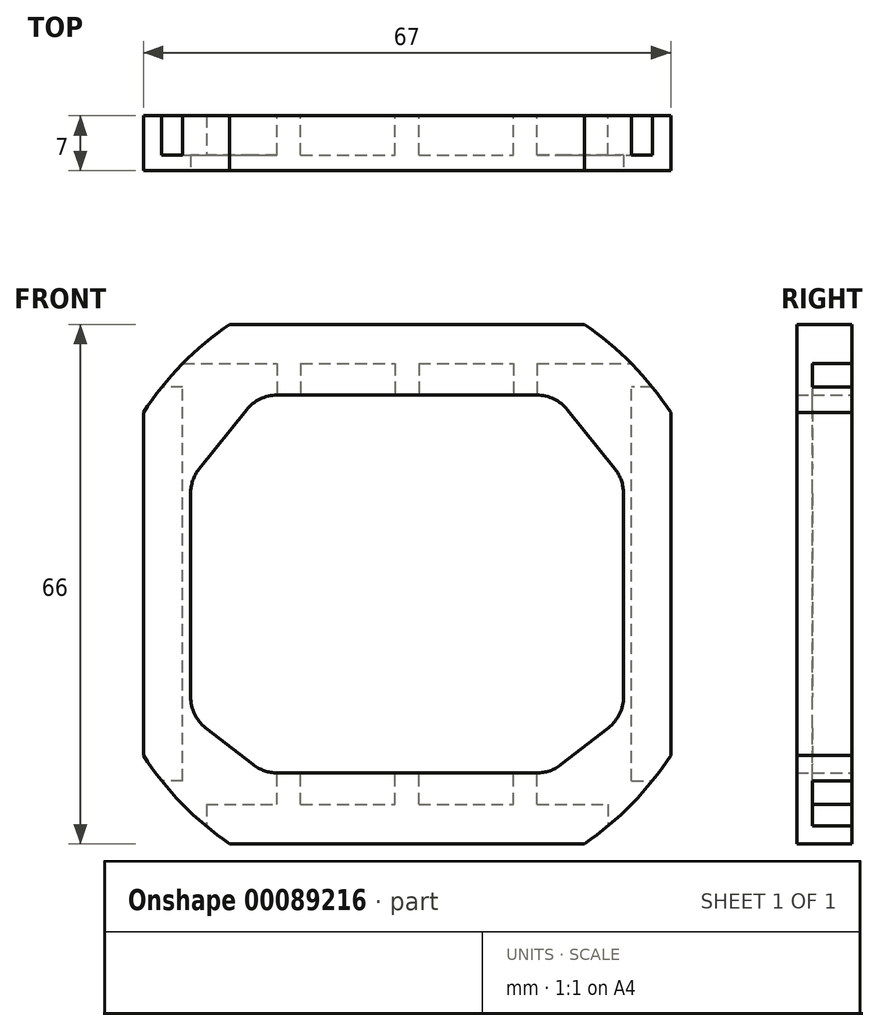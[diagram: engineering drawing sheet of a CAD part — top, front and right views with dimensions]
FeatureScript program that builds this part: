
annotation { "Feature Type Name" : "Feature", "Feature Type Description" : "" }
export const myFeature = defineFeature(function(context is Context, id is Id, definition is map)
    precondition{}
    {
        {
            var Q0;
            Q0=qCreatedBy(makeId("Front.planeOp"),FACE);
            var sketch = newSketch(context, id + "F0", { "sketchPlane" : qUnion([Q0])});
            skLineSegment(sketch, "E0.bottom", {"start": v(0, 0) * mm, "end": v(12, 0) * mm});
            skLineSegment(sketch, "E0.top", {"start": v(0, 56) * mm, "end": v(12, 56) * mm});
            skLineSegment(sketch, "E0.left", {"start": v(0, 0) * mm, "end": v(0, 56) * mm});
            skLineSegment(sketch, "E0.right", {"start": v(57, 0) * mm, "end": v(57, 56) * mm});
            skLineSegment(sketch, "E1.bottom", {"start": v(-5, 61) * mm, "end": v(62, 61) * mm});
            skLineSegment(sketch, "E1.top", {"start": v(-5, -5) * mm, "end": v(62, -5) * mm});
            skLineSegment(sketch, "E1.left", {"start": v(-5, 61) * mm, "end": v(-5, -5) * mm});
            skLineSegment(sketch, "E1.right", {"start": v(62, 61) * mm, "end": v(62, -5) * mm});
            skLineSegment(sketch, "E2.top", {"start": v(12, 52) * mm, "end": v(15, 52) * mm});
            skLineSegment(sketch, "E2.left", {"start": v(12, 56) * mm, "end": v(12, 52) * mm});
            skLineSegment(sketch, "E2.right", {"start": v(15, 56) * mm, "end": v(15, 52) * mm});
            skPoint(sketch, "E3.oppositeSnap0", {"position": v(30, 56) * mm});
            skLineSegment(sketch, "E3.top", {"start": v(27, 52) * mm, "end": v(30, 52) * mm});
            skLineSegment(sketch, "E3.left", {"start": v(27, 56) * mm, "end": v(27, 52) * mm});
            skLineSegment(sketch, "E3.right", {"start": v(30, 56) * mm, "end": v(30, 52) * mm});
            skLineSegment(sketch, "E4.top", {"start": v(42, 52) * mm, "end": v(45, 52) * mm});
            skLineSegment(sketch, "E4.left", {"start": v(42, 56) * mm, "end": v(42, 52) * mm});
            skLineSegment(sketch, "E4.right", {"start": v(45, 56) * mm, "end": v(45, 52) * mm});
            skLineSegment(sketch, "E5.top", {"start": v(12, 4) * mm, "end": v(15, 4) * mm});
            skLineSegment(sketch, "E5.left", {"start": v(12, 0) * mm, "end": v(12, 4) * mm});
            skLineSegment(sketch, "E5.right", {"start": v(15, 0) * mm, "end": v(15, 4) * mm});
            skLineSegment(sketch, "E6.top", {"start": v(27, 4) * mm, "end": v(30, 4) * mm});
            skLineSegment(sketch, "E6.left", {"start": v(27, 0) * mm, "end": v(27, 4) * mm});
            skLineSegment(sketch, "E6.right", {"start": v(30, 0) * mm, "end": v(30, 4) * mm});
            skLineSegment(sketch, "E7.top", {"start": v(42, 4) * mm, "end": v(45, 4) * mm});
            skLineSegment(sketch, "E7.left", {"start": v(42, 0) * mm, "end": v(42, 4) * mm});
            skLineSegment(sketch, "E7.right", {"start": v(45, 0) * mm, "end": v(45, 4) * mm});
            skLineSegment(sketch, "E8.trimOffspring", {"start": v(15, 56) * mm, "end": v(27, 56) * mm});
            skLineSegment(sketch, "E9.trimOffspring", {"start": v(30, 56) * mm, "end": v(42, 56) * mm});
            skLineSegment(sketch, "E10.trimOffspring", {"start": v(45, 56) * mm, "end": v(57, 56) * mm});
            skLineSegment(sketch, "E11.trimOffspring", {"start": v(30, 0) * mm, "end": v(42, 0) * mm});
            skLineSegment(sketch, "E12.trimOffspring", {"start": v(15, 0) * mm, "end": v(27, 0) * mm});
            skLineSegment(sketch, "E13.trimOffspring", {"start": v(45, 0) * mm, "end": v(57, 0) * mm});
            skSolve(sketch);
        }
        {
            var Q0;
            Q0=makeQuery(id+"F0.imprint","IMPRINT",FACE,{"disambiguationData":[TD([[makeQuery(id+"F0.imprint","IMPRINT",EDGE,{"derivedFrom":sQuery(id+"F0.wireOp",EDGE,"E0.bottom")}),-1.0]])]});
            extrude(context, id + "F1", {"entities" : qUnion([Q0]), "depth" : 5 * mm});
        }
        {
            var Q0;
            Q0=makeQuery(id+"F1.opExtrude","CAP_FACE",FACE,{"disambiguationData":[OSD([sQuery(id+"F0.wireOp",EDGE,"E0.bottom"),sQuery(id+"F0.wireOp",EDGE,"E0.top"),sQuery(id+"F0.wireOp",EDGE,"E0.left"),sQuery(id+"F0.wireOp",EDGE,"E0.right"),sQuery(id+"F0.wireOp",EDGE,"E1.bottom"),sQuery(id+"F0.wireOp",EDGE,"E1.top"),sQuery(id+"F0.wireOp",EDGE,"E1.left"),sQuery(id+"F0.wireOp",EDGE,"E1.right"),sQuery(id+"F0.wireOp",EDGE,"E2.top"),sQuery(id+"F0.wireOp",EDGE,"E2.left"),sQuery(id+"F0.wireOp",EDGE,"E2.right"),sQuery(id+"F0.wireOp",EDGE,"E3.top"),sQuery(id+"F0.wireOp",EDGE,"E3.left"),sQuery(id+"F0.wireOp",EDGE,"E3.right"),sQuery(id+"F0.wireOp",EDGE,"E4.top"),sQuery(id+"F0.wireOp",EDGE,"E4.left"),sQuery(id+"F0.wireOp",EDGE,"E4.right"),sQuery(id+"F0.wireOp",EDGE,"E5.top"),sQuery(id+"F0.wireOp",EDGE,"E5.left"),sQuery(id+"F0.wireOp",EDGE,"E5.right"),sQuery(id+"F0.wireOp",EDGE,"E6.top"),sQuery(id+"F0.wireOp",EDGE,"E6.left"),sQuery(id+"F0.wireOp",EDGE,"E6.right"),sQuery(id+"F0.wireOp",EDGE,"E7.top"),sQuery(id+"F0.wireOp",EDGE,"E7.left"),sQuery(id+"F0.wireOp",EDGE,"E7.right"),sQuery(id+"F0.wireOp",EDGE,"E8.trimOffspring"),sQuery(id+"F0.wireOp",EDGE,"E9.trimOffspring"),sQuery(id+"F0.wireOp",EDGE,"E10.trimOffspring"),sQuery(id+"F0.wireOp",EDGE,"E11.trimOffspring"),sQuery(id+"F0.wireOp",EDGE,"E12.trimOffspring"),sQuery(id+"F0.wireOp",EDGE,"E13.trimOffspring")])],"isStart":false});
            var sketch = newSketch(context, id + "F2", { "sketchPlane" : qUnion([Q0])});
            skLineSegment(sketch, "E14.bottom", {"start": v(-5, 61) * mm, "end": v(62, 61) * mm});
            skLineSegment(sketch, "E14.top", {"start": v(-5, -5) * mm, "end": v(62, -5) * mm});
            skLineSegment(sketch, "E14.left", {"start": v(-5, 61) * mm, "end": v(-5, -5) * mm});
            skLineSegment(sketch, "E14.right", {"start": v(62, 61) * mm, "end": v(62, -5) * mm});
            skLineSegment(sketch, "E15.bottom", {"start": v(12, 52) * mm, "end": v(15, 52) * mm});
            skLineSegment(sketch, "E15.top", {"start": v(12, 4) * mm, "end": v(15, 4) * mm});
            skLineSegment(sketch, "E15.left", {"start": v(12, 52) * mm, "end": v(12, 4) * mm});
            skLineSegment(sketch, "E15.right", {"start": v(15, 52) * mm, "end": v(15, 4) * mm});
            skLineSegment(sketch, "E16.bottom", {"start": v(27, 52) * mm, "end": v(30, 52) * mm});
            skLineSegment(sketch, "E16.top", {"start": v(27, 4) * mm, "end": v(30, 4) * mm});
            skLineSegment(sketch, "E16.left", {"start": v(27, 52) * mm, "end": v(27, 4) * mm});
            skLineSegment(sketch, "E16.right", {"start": v(30, 52) * mm, "end": v(30, 4) * mm});
            skLineSegment(sketch, "E17.bottom", {"start": v(42, 52) * mm, "end": v(45, 52) * mm});
            skLineSegment(sketch, "E17.top", {"start": v(42, 4) * mm, "end": v(45, 4) * mm});
            skLineSegment(sketch, "E17.left", {"start": v(42, 52) * mm, "end": v(42, 4) * mm});
            skLineSegment(sketch, "E17.right", {"start": v(45, 52) * mm, "end": v(45, 4) * mm});
            skSolve(sketch);
        }
        {
            var Q0;
            Q0=makeQuery(id+"F2.imprint","IMPRINT",FACE,{"disambiguationData":[TD([[makeQuery(id+"F2.imprint","IMPRINT",EDGE,{"derivedFrom":sQuery(id+"F2.wireOp",EDGE,"E14.bottom")}),-1.0]])]});
            var Q1;
            Q1=makeQuery(id+"F2.imprint","IMPRINT",FACE,{"disambiguationData":[TD([[makeQuery(id+"F2.imprint","IMPRINT",EDGE,{"derivedFrom":sQuery(id+"F2.wireOp",EDGE,"E15.left")}),-1.0]])]});
            var Q2;
            Q2=makeQuery(id+"F2.imprint","IMPRINT",FACE,{"disambiguationData":[TD([[makeQuery(id+"F2.imprint","IMPRINT",EDGE,{"derivedFrom":sQuery(id+"F2.wireOp",EDGE,"E15.right")}),1.0]])]});
            var Q3;
            Q3=makeQuery(id+"F2.imprint","IMPRINT",FACE,{"disambiguationData":[TD([[makeQuery(id+"F2.imprint","IMPRINT",EDGE,{"derivedFrom":sQuery(id+"F2.wireOp",EDGE,"E16.right")}),1.0]])]});
            var Q4;
            Q4=makeQuery(id+"F2.imprint","IMPRINT",FACE,{"disambiguationData":[TD([[makeQuery(id+"F2.imprint","IMPRINT",EDGE,{"derivedFrom":sQuery(id+"F2.wireOp",EDGE,"E17.right")}),1.0]])]});
            extrude(context, id + "F3", {"entities" : qUnion([Q0, Q1, Q2, Q3, Q4]), "operationType" : NewBodyOperationType.ADD, "depth" : 2 * mm});
        }
        {
            var Q0;
            Q0=makeQuery(id+"F3.opExtrude","CAP_FACE",FACE,{"disambiguationData":[OSD([sQuery(id+"F2.wireOp",EDGE,"E14.bottom"),sQuery(id+"F2.wireOp",EDGE,"E14.top"),sQuery(id+"F2.wireOp",EDGE,"E14.left"),sQuery(id+"F2.wireOp",EDGE,"E14.right"),sQuery(id+"F2.wireOp",EDGE,"E15.bottom"),sQuery(id+"F2.wireOp",EDGE,"E15.top"),sQuery(id+"F2.wireOp",EDGE,"E15.left"),sQuery(id+"F2.wireOp",EDGE,"E15.right"),sQuery(id+"F2.wireOp",EDGE,"E16.bottom"),sQuery(id+"F2.wireOp",EDGE,"E16.top"),sQuery(id+"F2.wireOp",EDGE,"E16.left"),sQuery(id+"F2.wireOp",EDGE,"E16.right"),sQuery(id+"F2.wireOp",EDGE,"E17.bottom"),sQuery(id+"F2.wireOp",EDGE,"E17.top"),sQuery(id+"F2.wireOp",EDGE,"E17.left"),sQuery(id+"F2.wireOp",EDGE,"E17.right")])],"isStart":false});
            var sketch = newSketch(context, id + "F4", { "sketchPlane" : qUnion([Q0])});
            skLineSegment(sketch, "E18.left", {"start": v(56, 39.5) * mm, "end": v(56, 13.7) * mm});
            skLineSegment(sketch, "E19.right", {"start": v(1, 39.5) * mm, "end": v(1, 13.7) * mm});
            skPoint(sketch, "E20.visualSharp", {"position": v(1, 41) * mm});
            skPoint(sketch, "E21.visualSharp", {"position": v(10, 41) * mm});
            skPoint(sketch, "E22.visualSharp", {"position": v(10, 19) * mm});
            skPoint(sketch, "E23.visualSharp", {"position": v(1, 19) * mm});
            skPoint(sketch, "E24.visualSharp", {"position": v(17.5, 41) * mm});
            skPoint(sketch, "E25.visualSharp", {"position": v(26.5, 41) * mm});
            skPoint(sketch, "E26.visualSharp", {"position": v(26.5, 19) * mm});
            skPoint(sketch, "E27.visualSharp", {"position": v(17.5, 19) * mm});
            skPoint(sketch, "E28.visualSharp", {"position": v(33.5, 19) * mm});
            skPoint(sketch, "E29.visualSharp", {"position": v(42.5, 19) * mm});
            skPoint(sketch, "E30.visualSharp", {"position": v(42.5, 41) * mm});
            skPoint(sketch, "E31.visualSharp", {"position": v(33.5, 41) * mm});
            skPoint(sketch, "E32.visualSharp", {"position": v(49.5, 41) * mm});
            skPoint(sketch, "E33.visualSharp", {"position": v(56, 19) * mm});
            skPoint(sketch, "E34.visualSharp", {"position": v(56, 41) * mm});
            skPoint(sketch, "E35.visualSharp", {"position": v(49.5, 19) * mm});
            skLineSegment(sketch, "E36", {"start": v(2.1, 42.62) * mm, "end": v(8.1, 50.12) * mm});
            skLineSegment(sketch, "E37", {"start": v(12, 52) * mm, "end": v(45, 52) * mm});
            skLineSegment(sketch, "E38", {"start": v(48.9, 50.12) * mm, "end": v(54.9, 42.62) * mm});
            skLineSegment(sketch, "E39", {"start": v(54.08, 9.75) * mm, "end": v(48.08, 5.06) * mm});
            skLineSegment(sketch, "E40", {"start": v(45, 4) * mm, "end": v(12, 4) * mm});
            skLineSegment(sketch, "E41", {"start": v(8.92, 5.06) * mm, "end": v(2.92, 9.75) * mm});
            skPoint(sketch, "E42.visualSharp", {"position": v(1, 41.25) * mm});
            skArc(sketch, "E42.filletArc", {"start": v(2.1, 42.62) * mm, "mid": v(1.28, 41.16) * mm, "end": v(1, 39.5) * mm});
            skPoint(sketch, "E43.visualSharp", {"position": v(1, 11.25) * mm});
            skArc(sketch, "E43.filletArc", {"start": v(1, 13.7) * mm, "mid": v(1.5, 11.5) * mm, "end": v(2.92, 9.75) * mm});
            skPoint(sketch, "E44.visualSharp", {"position": v(56, 41.25) * mm});
            skArc(sketch, "E44.filletArc", {"start": v(56, 39.5) * mm, "mid": v(55.72, 41.16) * mm, "end": v(54.9, 42.62) * mm});
            skPoint(sketch, "E45.visualSharp", {"position": v(56, 11.25) * mm});
            skArc(sketch, "E45.filletArc", {"start": v(54.08, 9.75) * mm, "mid": v(55.5, 11.5) * mm, "end": v(56, 13.7) * mm});
            skArc(sketch, "E46.filletArc", {"start": v(48.9, 50.12) * mm, "mid": v(47.17, 51.5) * mm, "end": v(45, 52) * mm});
            skArc(sketch, "E47.filletArc", {"start": v(12, 52) * mm, "mid": v(9.83, 51.5) * mm, "end": v(8.1, 50.12) * mm});
            skArc(sketch, "E48.filletArc", {"start": v(8.92, 5.06) * mm, "mid": v(10.37, 4.27) * mm, "end": v(12, 4) * mm});
            skArc(sketch, "E49.filletArc", {"start": v(45, 4) * mm, "mid": v(46.63, 4.27) * mm, "end": v(48.08, 5.06) * mm});
            skSolve(sketch);
        }
        {
            var Q0;
            Q0=makeQuery(id+"F4.imprint","IMPRINT",FACE,{"disambiguationData":[TD([[makeQuery(id+"F4.imprint","IMPRINT",EDGE,{"derivedFrom":sQuery(id+"F4.wireOp",EDGE,"E19.right")}),1.0]])]});
            var Q1;
            {var subQ1=makeQuery(id+"F3.opExtrude","CAP_EDGE",EDGE,{"disambiguationData":[OSD([sQuery(id+"F2.wireOp",EDGE,"E15.right")])],"isStart":false});Q1=makeQuery(id+"F4.imprint","IMPRINT",FACE,{"disambiguationData":[TD([[makeQuery(id+"F4.imprint","IMPRINT",EDGE,{"derivedFrom":subQ1}),1.0]])]});}
            var Q2;
            {var subQ1=makeQuery(id+"F3.opExtrude","CAP_EDGE",EDGE,{"disambiguationData":[OSD([sQuery(id+"F2.wireOp",EDGE,"E16.right")])],"isStart":false});Q2=makeQuery(id+"F4.imprint","IMPRINT",FACE,{"disambiguationData":[TD([[makeQuery(id+"F4.imprint","IMPRINT",EDGE,{"derivedFrom":subQ1}),1.0]])]});}
            var Q3;
            Q3=makeQuery(id+"F4.imprint","IMPRINT",FACE,{"disambiguationData":[TD([[makeQuery(id+"F4.imprint","IMPRINT",EDGE,{"derivedFrom":sQuery(id+"F4.wireOp",EDGE,"E18.left")}),-1.0]])]});
            extrude(context, id + "F5", {"entities" : qUnion([Q0, Q1, Q2, Q3]), "operationType" : NewBodyOperationType.REMOVE, "endBound" : BoundingType.THROUGH_ALL, "oppositeDirection" : true, "depth" : 25 * mm});
        }
        {
            var Q0;
            Q0=makeQuery(id+"F3.opExtrude","CAP_FACE",FACE,{"disambiguationData":[OSD([sQuery(id+"F2.wireOp",EDGE,"E14.bottom"),sQuery(id+"F2.wireOp",EDGE,"E14.top"),sQuery(id+"F2.wireOp",EDGE,"E14.left"),sQuery(id+"F2.wireOp",EDGE,"E14.right"),sQuery(id+"F2.wireOp",EDGE,"E15.bottom"),sQuery(id+"F2.wireOp",EDGE,"E15.top"),sQuery(id+"F2.wireOp",EDGE,"E15.left"),sQuery(id+"F2.wireOp",EDGE,"E15.right"),sQuery(id+"F2.wireOp",EDGE,"E16.bottom"),sQuery(id+"F2.wireOp",EDGE,"E16.top"),sQuery(id+"F2.wireOp",EDGE,"E16.left"),sQuery(id+"F2.wireOp",EDGE,"E16.right"),sQuery(id+"F2.wireOp",EDGE,"E17.bottom"),sQuery(id+"F2.wireOp",EDGE,"E17.top"),sQuery(id+"F2.wireOp",EDGE,"E17.left"),sQuery(id+"F2.wireOp",EDGE,"E17.right")])],"isStart":false});
            var sketch = newSketch(context, id + "F6", { "sketchPlane" : qUnion([Q0])});
            skArc(sketch, "E50", {"start": v(5.98, 61) * mm, "mid": v(-0.07, 55.93) * mm, "end": v(-5, 49.77) * mm});
            skLineSegment(sketch, "E51", {"start": v(-5, 49.77) * mm, "end": v(-5, 6.23) * mm});
            skLineSegment(sketch, "E52", {"start": v(5.98, 61) * mm, "end": v(51.02, 61) * mm});
            skLineSegment(sketch, "E53", {"start": v(62, 49.77) * mm, "end": v(62, 6.23) * mm});
            skLineSegment(sketch, "E54", {"start": v(5.98, -5) * mm, "end": v(51.02, -5) * mm});
            skArc(sketch, "E55.trimOffspring", {"start": v(-5, 6.23) * mm, "mid": v(-0.07, 0.07) * mm, "end": v(5.98, -5) * mm});
            skArc(sketch, "E56.trimOffspring", {"start": v(51.02, -5) * mm, "mid": v(57.07, 0.07) * mm, "end": v(62, 6.23) * mm});
            skArc(sketch, "E57.trimOffspring", {"start": v(62, 49.77) * mm, "mid": v(57.07, 55.93) * mm, "end": v(51.02, 61) * mm});
            skSolve(sketch);
        }
        {
            var Q0;
            {var subQ0=sQuery(id+"F6.wireOp",EDGE,"E50");Q0=makeQuery(id+"F6.imprint","IMPRINT",FACE,{"disambiguationData":[TD([[makeQuery(id+"F6.imprint","IMPRINT",EDGE,{"derivedFrom":subQ0}),-1.0]])]});}
            var Q1;
            {var subQ0=sQuery(id+"F6.wireOp",EDGE,"E57.trimOffspring");Q1=makeQuery(id+"F6.imprint","IMPRINT",FACE,{"disambiguationData":[TD([[makeQuery(id+"F6.imprint","IMPRINT",EDGE,{"derivedFrom":subQ0}),-1.0]])]});}
            var Q2;
            {var subQ0=sQuery(id+"F6.wireOp",EDGE,"E56.trimOffspring");Q2=makeQuery(id+"F6.imprint","IMPRINT",FACE,{"disambiguationData":[TD([[makeQuery(id+"F6.imprint","IMPRINT",EDGE,{"derivedFrom":subQ0}),-1.0]])]});}
            var Q3;
            {var subQ0=sQuery(id+"F6.wireOp",EDGE,"E55.trimOffspring");Q3=makeQuery(id+"F6.imprint","IMPRINT",FACE,{"disambiguationData":[TD([[makeQuery(id+"F6.imprint","IMPRINT",EDGE,{"derivedFrom":subQ0}),-1.0]])]});}
            extrude(context, id + "F7", {"entities" : qUnion([Q0, Q1, Q2, Q3]), "operationType" : NewBodyOperationType.REMOVE, "endBound" : BoundingType.THROUGH_ALL, "oppositeDirection" : true, "depth" : 25 * mm});
        }
        {
            var Q0;
            {var subQ0=sQuery(id+"F0.wireOp",EDGE,"E4.left");var subQ1=sQuery(id+"F0.wireOp",EDGE,"E2.top");var subQ2=sQuery(id+"F0.wireOp",EDGE,"E8.trimOffspring");var subQ3=sQuery(id+"F0.wireOp",EDGE,"E4.top");var subQ4=sQuery(id+"F0.wireOp",EDGE,"E3.right");var subQ5=sQuery(id+"F0.wireOp",EDGE,"E3.left");var subQ6=sQuery(id+"F0.wireOp",EDGE,"E3.top");var subQ7=sQuery(id+"F0.wireOp",EDGE,"E2.right");var subQ8=sQuery(id+"F0.wireOp",EDGE,"E1.bottom");var subQ9=sQuery(id+"F0.wireOp",EDGE,"E0.top");var subQ10=sQuery(id+"F0.wireOp",EDGE,"E2.left");var subQ11=sQuery(id+"F0.wireOp",EDGE,"E4.right");var subQ12=sQuery(id+"F0.wireOp",EDGE,"E9.trimOffspring");var subQ13=sQuery(id+"F0.wireOp",EDGE,"E10.trimOffspring");Q0=makeQuery(id+"F7.boolean.opBoolean","SPLIT",FACE,{"disambiguationData":[TD([makeQuery(id+"F1.opExtrude","SWEPT_FACE",FACE,{"disambiguationData":[OSD([subQ9])]})])],"derivedFrom":makeQuery(id+"F1.opExtrude","CAP_FACE",FACE,{"disambiguationData":[OSD([sQuery(id+"F0.wireOp",EDGE,"E0.bottom"),subQ9,sQuery(id+"F0.wireOp",EDGE,"E0.left"),sQuery(id+"F0.wireOp",EDGE,"E0.right"),subQ8,sQuery(id+"F0.wireOp",EDGE,"E1.top"),sQuery(id+"F0.wireOp",EDGE,"E1.left"),sQuery(id+"F0.wireOp",EDGE,"E1.right"),subQ1,subQ10,subQ7,subQ6,subQ5,subQ4,subQ3,subQ0,subQ11,sQuery(id+"F0.wireOp",EDGE,"E5.top"),sQuery(id+"F0.wireOp",EDGE,"E5.left"),sQuery(id+"F0.wireOp",EDGE,"E5.right"),sQuery(id+"F0.wireOp",EDGE,"E6.top"),sQuery(id+"F0.wireOp",EDGE,"E6.left"),sQuery(id+"F0.wireOp",EDGE,"E6.right"),sQuery(id+"F0.wireOp",EDGE,"E7.top"),sQuery(id+"F0.wireOp",EDGE,"E7.left"),sQuery(id+"F0.wireOp",EDGE,"E7.right"),subQ2,subQ12,subQ13,sQuery(id+"F0.wireOp",EDGE,"E11.trimOffspring"),sQuery(id+"F0.wireOp",EDGE,"E12.trimOffspring"),sQuery(id+"F0.wireOp",EDGE,"E13.trimOffspring")])],"isStart":true})});}
            var sketch = newSketch(context, id + "F8", { "sketchPlane" : qUnion([Q0])});
            skLineSegment(sketch, "E58.bottom", {"start": v(-60, 59) * mm, "end": v(-54, 59) * mm});
            skLineSegment(sketch, "E58.top", {"start": v(-60, 53) * mm, "end": v(-54, 53) * mm});
            skLineSegment(sketch, "E58.left", {"start": v(-60, 59) * mm, "end": v(-60, 53) * mm});
            skLineSegment(sketch, "E58.right", {"start": v(-54, 59) * mm, "end": v(-54, 53) * mm});
            skLineSegment(sketch, "E59.bottom", {"start": v(-3, 53) * mm, "end": v(3, 53) * mm});
            skLineSegment(sketch, "E59.top", {"start": v(-3, 59) * mm, "end": v(3, 59) * mm});
            skLineSegment(sketch, "E59.left", {"start": v(-3, 53) * mm, "end": v(-3, 59) * mm});
            skLineSegment(sketch, "E59.right", {"start": v(3, 53) * mm, "end": v(3, 59) * mm});
            skLineSegment(sketch, "E60.bottom", {"start": v(-3, 3) * mm, "end": v(3, 3) * mm});
            skLineSegment(sketch, "E60.top", {"start": v(-3, -3) * mm, "end": v(3, -3) * mm});
            skLineSegment(sketch, "E60.left", {"start": v(-3, 3) * mm, "end": v(-3, -3) * mm});
            skLineSegment(sketch, "E60.right", {"start": v(3, 3) * mm, "end": v(3, -3) * mm});
            skLineSegment(sketch, "E61.bottom", {"start": v(-54, 3) * mm, "end": v(-60, 3) * mm});
            skLineSegment(sketch, "E61.top", {"start": v(-54, -3) * mm, "end": v(-60, -3) * mm});
            skLineSegment(sketch, "E61.left", {"start": v(-54, 3) * mm, "end": v(-54, -3) * mm});
            skLineSegment(sketch, "E61.right", {"start": v(-60, 3) * mm, "end": v(-60, -3) * mm});
            skSolve(sketch);
        }
        {
            var Q0;
            {var subQ1=sQuery(id+"F8.wireOp",EDGE,"E58.bottom");Q0=makeQuery(id+"F8.imprint","IMPRINT",FACE,{"disambiguationData":[TD([[makeQuery(id+"F8.imprint","IMPRINT",EDGE,{"derivedFrom":subQ1}),-1.0]])]});}
            var Q1;
            {var subQ5=sQuery(id+"F8.wireOp",EDGE,"E59.bottom");Q1=makeQuery(id+"F8.imprint","IMPRINT",FACE,{"disambiguationData":[TD([[makeQuery(id+"F8.imprint","IMPRINT",EDGE,{"derivedFrom":subQ5}),1.0]])]});}
            var Q2;
            Q2=makeQuery(id+"F8.imprint","IMPRINT",FACE,{"disambiguationData":[TD([[makeQuery(id+"F8.imprint","IMPRINT",EDGE,{"derivedFrom":sQuery(id+"F8.wireOp",EDGE,"E60.bottom")}),-1.0]])]});
            var Q3;
            Q3=makeQuery(id+"F8.imprint","IMPRINT",FACE,{"disambiguationData":[TD([[makeQuery(id+"F8.imprint","IMPRINT",EDGE,{"derivedFrom":sQuery(id+"F8.wireOp",EDGE,"E61.bottom")}),1.0]])]});
            var Q4;
            {var subQ0=sQuery(id+"F2.wireOp",EDGE,"E17.bottom");var subQ1=sQuery(id+"F2.wireOp",EDGE,"E17.top");var subQ2=sQuery(id+"F2.wireOp",EDGE,"E17.right");Q4=makeQuery(id+"F3.boolean.opBoolean","SPLIT",FACE,{"disambiguationData":[TD([makeQuery(id+"F1.opExtrude","SWEPT_FACE",FACE,{"disambiguationData":[OSD([sQuery(id+"F0.wireOp",EDGE,"E0.right")])]})])],"derivedFrom":makeQuery(id+"F3.opExtrude","CAP_FACE",FACE,{"disambiguationData":[OSD([sQuery(id+"F2.wireOp",EDGE,"E14.bottom"),sQuery(id+"F2.wireOp",EDGE,"E14.top"),sQuery(id+"F2.wireOp",EDGE,"E14.left"),sQuery(id+"F2.wireOp",EDGE,"E14.right"),sQuery(id+"F2.wireOp",EDGE,"E15.bottom"),sQuery(id+"F2.wireOp",EDGE,"E15.top"),sQuery(id+"F2.wireOp",EDGE,"E15.left"),sQuery(id+"F2.wireOp",EDGE,"E15.right"),sQuery(id+"F2.wireOp",EDGE,"E16.bottom"),sQuery(id+"F2.wireOp",EDGE,"E16.top"),sQuery(id+"F2.wireOp",EDGE,"E16.left"),sQuery(id+"F2.wireOp",EDGE,"E16.right"),subQ0,subQ1,sQuery(id+"F2.wireOp",EDGE,"E17.left"),subQ2])],"isStart":true})});}
            extrude(context, id + "F9", {"entities" : qUnion([Q0, Q1, Q2, Q3]), "operationType" : NewBodyOperationType.REMOVE, "oppositeDirection" : true, "endBoundEntityFace" : qUnion([Q4]), "depth" : 5 * mm});
        }
    });
